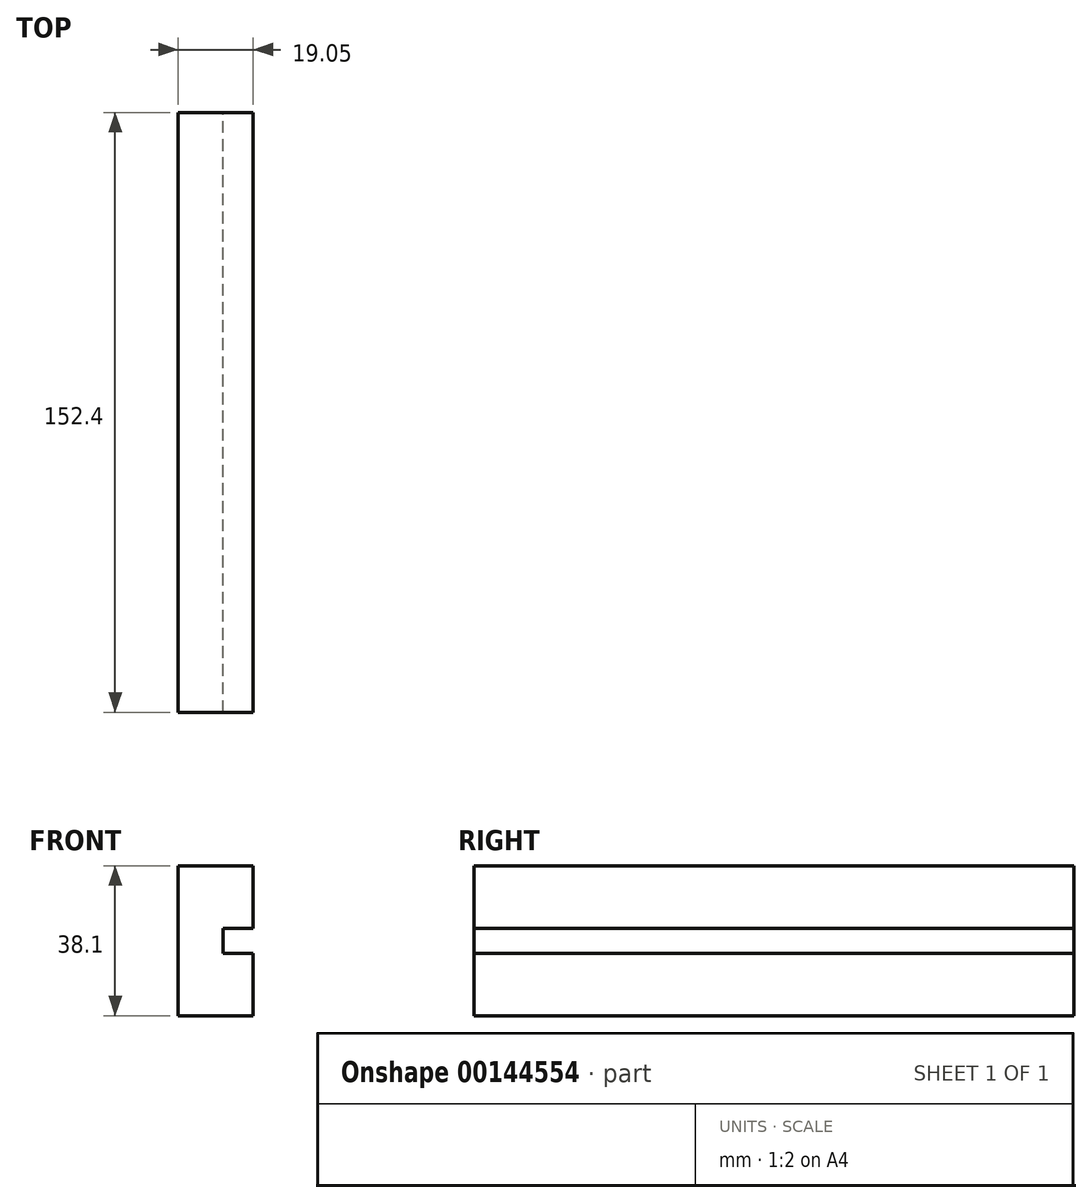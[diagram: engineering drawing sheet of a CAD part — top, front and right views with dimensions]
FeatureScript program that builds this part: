
annotation { "Feature Type Name" : "Feature", "Feature Type Description" : "" }
export const myFeature = defineFeature(function(context is Context, id is Id, definition is map)
    precondition{}
    {
        {
            var Q0;
            Q0=qCreatedBy(makeId("Front.planeOp"),FACE);
            var sketch = newSketch(context, id + "F0", { "sketchPlane" : qUnion([Q0])});
            skLineSegment(sketch, "E0.bottom", {"start": v(-27.57, -4.33) * mm, "end": v(-8.52, -4.33) * mm});
            skLineSegment(sketch, "E0.top", {"start": v(-27.57, -42.43) * mm, "end": v(-8.52, -42.43) * mm});
            skLineSegment(sketch, "E0.left", {"start": v(-27.57, -4.33) * mm, "end": v(-27.57, -42.43) * mm});
            skLineSegment(sketch, "E1", {"start": v(-8.52, -26.56) * mm, "end": v(-8.52, -42.43) * mm});
            skLineSegment(sketch, "E2", {"start": v(-8.52, -20.2) * mm, "end": v(-8.52, -4.33) * mm});
            skLineSegment(sketch, "E3", {"start": v(-8.52, -20.2) * mm, "end": v(-16.14, -20.2) * mm});
            skLineSegment(sketch, "E4.bottom", {"start": v(-16.14, -20.2) * mm, "end": v(-8.52, -20.2) * mm});
            skLineSegment(sketch, "E4.top", {"start": v(-16.14, -26.56) * mm, "end": v(-8.52, -26.56) * mm});
            skLineSegment(sketch, "E4.left", {"start": v(-16.14, -20.2) * mm, "end": v(-16.14, -26.56) * mm});
            skSolve(sketch);
        }
        {
            var Q0;
            Q0=makeQuery(id+"F0.imprint","IMPRINT",FACE,{"disambiguationData":[TD([[makeQuery(id+"F0.imprint","IMPRINT",EDGE,{"derivedFrom":sQuery(id+"F0.wireOp",EDGE,"E0.bottom")}),-1.0]])]});
            extrude(context, id + "F1", {"entities" : qUnion([Q0]), "depth" : 152.4 * mm});
        }
    });
